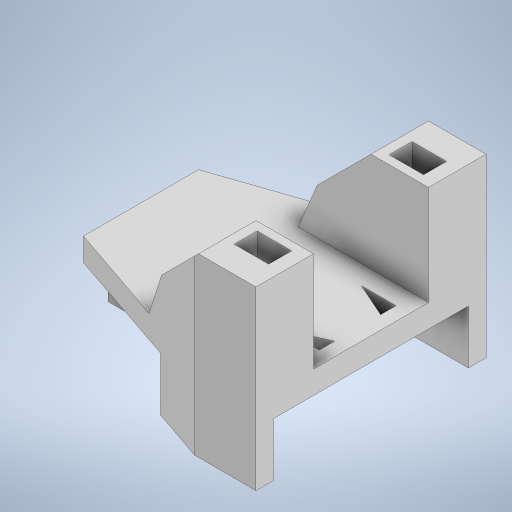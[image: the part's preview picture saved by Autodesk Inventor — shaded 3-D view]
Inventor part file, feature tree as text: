
AUTODESK INVENTOR PART (.ipt)
format: ipt  version: 2024.2 (Build 282272000, 272)  size: 369,152 bytes
history: native  units: mm
features: extrude x7, sketch x7, chamfer x2, fillet x1
ambient origin geometry x8: Origin, YZ Plane, XZ Plane, XY Plane, X Axis, Y Axis, Z Axis, Center Point
bodies: Solid1 (feature_tree)
feature tree (17):
  extrude  "Extrusion1"  Depth=2.3mm
  extrude  "Extrusion2"  Depth=7.0mm TaperAngle=0.0deg
  extrude  "Extrusion3"  Depth=3.0mm
  fillet  "Fillet1"  Radius=24.0mm
  extrude  "Extrusion4"  Depth=0.2mm
  extrude  "Extrusion5"  Depth=4.0mm
  extrude  "Extrusion7"  Depth=15.0mm
  chamfer  "Chamfer1"  Distance=4.0mm
  chamfer  "Chamfer2"  Distance=3.0mm
  extrude  "Extrusion10"  Depth=2.0mm
  sketch  "Sketch1"  dims[d0=30.0mm d1=8.0mm d2=4.5mm d3=3.0mm d4=3.0mm d5=17.2mm d6=3.4mm d7=1.75mm d8=15.0mm d9=7.5mm d10=22.0mm d11=22.0mm d12=3.0mm d13=0.0mm d14=2.3mm]
  sketch  "Sketch2"  dims[d15=2.3mm d24=7.0mm d25=0.0mm]
  sketch  "Sketch3"  dims[d26=14.746667mm d27=3.0mm d28=24.0mm]
  sketch  "Sketch4"  dims[d29=14.6mm d30=0.2mm]
  sketch  "Sketch5"  dims[d31=2.8mm d32=4.0mm]
  sketch  "Sketch6"  dims[d33=7.0mm d34=15.0mm d35=4.0mm d36=0.0mm]
  sketch  "Sketch9"  dims[d37=2.0mm d38=3.0mm d39=2.0mm d40=2.0mm d41=3.0mm d42=5.0mm d43=0.0mm d44=6.0mm d45=15.5mm d46=5.0mm d47=5.0mm d48=0.0mm d52=3.0mm d55=17.0mm d56=1.1mm d57=17.0mm d58=1.1mm d59=13.0mm d60=0.0mm d61=9.5mm d62=2.0mm d63=45.0deg d64=3.5mm d65=2.0mm d66=45.0deg d84=1.0mm d85=0.0mm d86=0.5mm d87=0.872665mm]
